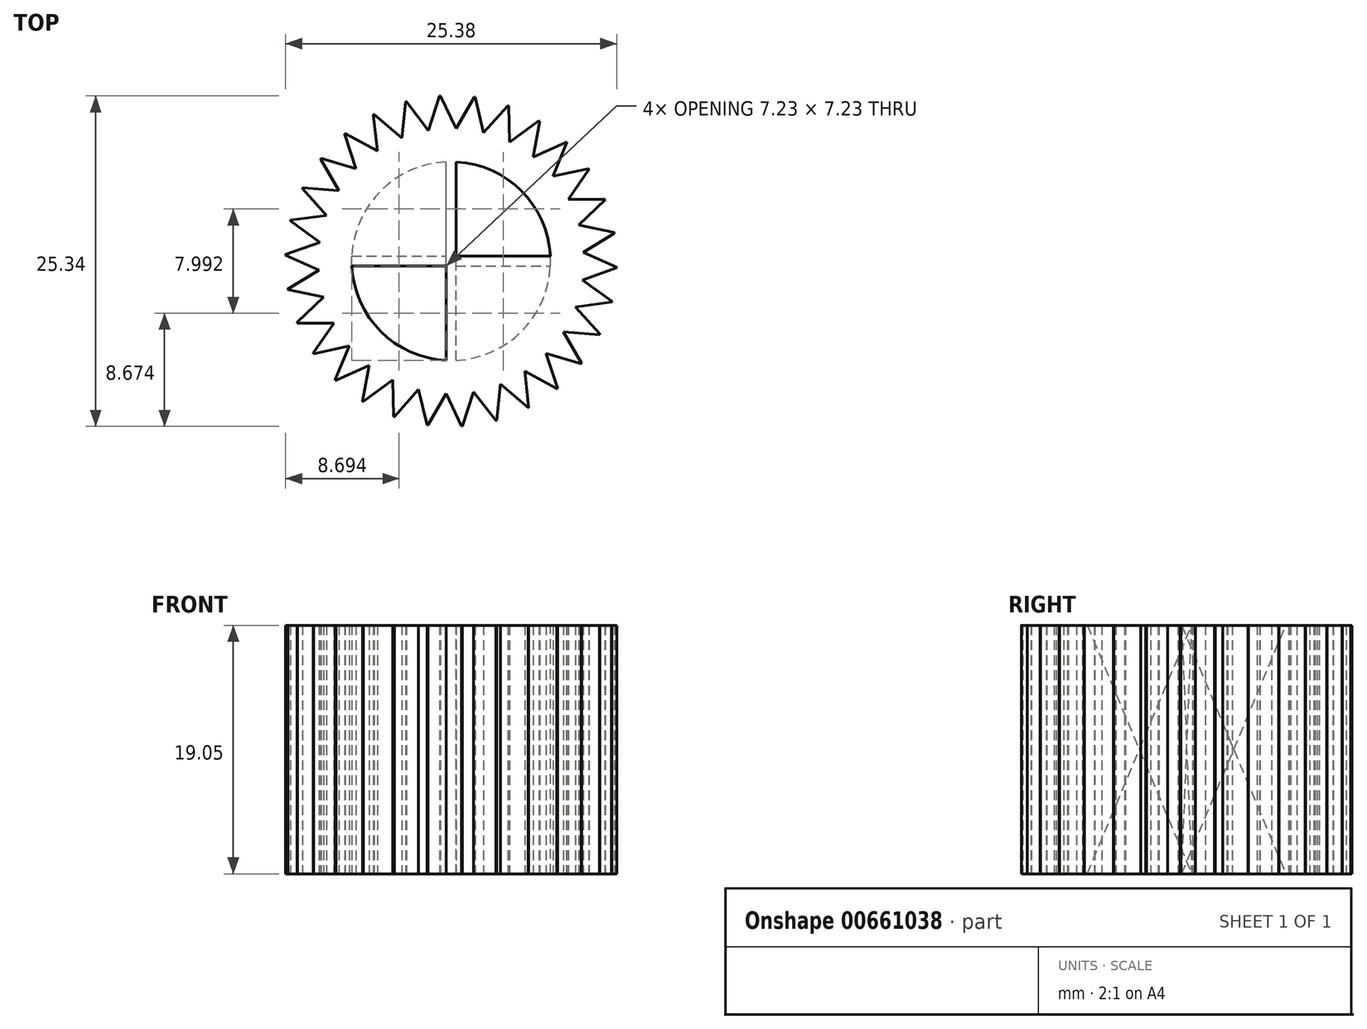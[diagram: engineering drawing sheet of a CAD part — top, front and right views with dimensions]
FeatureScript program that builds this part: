
annotation { "Feature Type Name" : "Feature", "Feature Type Description" : "" }
export const myFeature = defineFeature(function(context is Context, id is Id, definition is map)
    precondition{}
    {
        {
            var Q0;
            Q0=qCreatedBy(makeId("Top.planeOp"),FACE);
            var sketch = newSketch(context, id + "F0", { "sketchPlane" : qUnion([Q0])});
            skCircle(sketch, "E0", {"center": v(0, 0) * mm, "radius": 12.7 * mm});
            skCircle(sketch, "E1", {"center": v(0, 0) * mm, "radius": 10.16 * mm});
            skLineSegment(sketch, "E2", {"start": v(-3.43, 12.23) * mm, "end": v(-1.73, 10.01) * mm});
            skLineSegment(sketch, "E3", {"start": v(-1.73, 10.01) * mm, "end": v(-0.87, 12.67) * mm});
            skLineSegment(sketch, "E4.1.0", {"start": v(-3.78, 9.43) * mm, "end": v(-3.49, 12.21) * mm});
            skLineSegment(sketch, "E4.1.1", {"start": v(-5.9, 11.25) * mm, "end": v(-3.78, 9.43) * mm});
            skLineSegment(sketch, "E4.2.0", {"start": v(-5.65, 8.44) * mm, "end": v(-5.95, 11.22) * mm});
            skLineSegment(sketch, "E4.2.1", {"start": v(-8.11, 9.77) * mm, "end": v(-5.65, 8.44) * mm});
            skLineSegment(sketch, "E4.3.0", {"start": v(-7.29, 7.08) * mm, "end": v(-8.15, 9.74) * mm});
            skLineSegment(sketch, "E4.3.1", {"start": v(-9.96, 7.87) * mm, "end": v(-7.29, 7.08) * mm});
            skLineSegment(sketch, "E4.4.0", {"start": v(-8.6, 5.41) * mm, "end": v(-10, 7.83) * mm});
            skLineSegment(sketch, "E4.4.1", {"start": v(-11.38, 5.63) * mm, "end": v(-8.6, 5.41) * mm});
            skLineSegment(sketch, "E4.5.0", {"start": v(-9.54, 3.5) * mm, "end": v(-11.4, 5.58) * mm});
            skLineSegment(sketch, "E4.5.1", {"start": v(-12.3, 3.14) * mm, "end": v(-9.54, 3.5) * mm});
            skLineSegment(sketch, "E4.6.0", {"start": v(-10.06, 1.45) * mm, "end": v(-12.32, 3.09) * mm});
            skLineSegment(sketch, "E4.6.1", {"start": v(-12.69, 0.51) * mm, "end": v(-10.06, 1.45) * mm});
            skLineSegment(sketch, "E4.7.0", {"start": v(-10.14, -0.68) * mm, "end": v(-12.7, 0.46) * mm});
            skLineSegment(sketch, "E4.7.1", {"start": v(-12.52, -2.14) * mm, "end": v(-10.14, -0.68) * mm});
            skLineSegment(sketch, "E4.8.0", {"start": v(-9.78, -2.77) * mm, "end": v(-12.5, -2.2) * mm});
            skLineSegment(sketch, "E4.8.1", {"start": v(-11.8, -4.7) * mm, "end": v(-9.78, -2.77) * mm});
            skLineSegment(sketch, "E4.9.0", {"start": v(-8.99, -4.74) * mm, "end": v(-11.78, -4.74) * mm});
            skLineSegment(sketch, "E4.9.1", {"start": v(-10.57, -7.04) * mm, "end": v(-8.99, -4.74) * mm});
            skLineSegment(sketch, "E4.10.0", {"start": v(-7.8, -6.5) * mm, "end": v(-10.54, -7.1) * mm});
            skLineSegment(sketch, "E4.10.1", {"start": v(-8.87, -9.09) * mm, "end": v(-7.8, -6.5) * mm});
            skLineSegment(sketch, "E4.11.0", {"start": v(-6.28, -7.99) * mm, "end": v(-8.83, -9.13) * mm});
            skLineSegment(sketch, "E4.11.1", {"start": v(-6.79, -10.73) * mm, "end": v(-6.28, -7.99) * mm});
            skLineSegment(sketch, "E4.12.0", {"start": v(-4.48, -9.12) * mm, "end": v(-6.74, -10.76) * mm});
            skLineSegment(sketch, "E4.12.1", {"start": v(-4.4, -11.91) * mm, "end": v(-4.48, -9.12) * mm});
            skLineSegment(sketch, "E4.13.0", {"start": v(-2.5, -9.85) * mm, "end": v(-4.36, -11.93) * mm});
            skLineSegment(sketch, "E4.13.1", {"start": v(-1.84, -12.57) * mm, "end": v(-2.5, -9.85) * mm});
            skLineSegment(sketch, "E4.14.0", {"start": v(-0.39, -10.15) * mm, "end": v(-1.78, -12.57) * mm});
            skLineSegment(sketch, "E4.14.1", {"start": v(0.82, -12.67) * mm, "end": v(-0.39, -10.15) * mm});
            skLineSegment(sketch, "E4.15.0", {"start": v(1.73, -10.01) * mm, "end": v(0.87, -12.67) * mm});
            skLineSegment(sketch, "E4.15.1", {"start": v(3.43, -12.23) * mm, "end": v(1.73, -10.01) * mm});
            skLineSegment(sketch, "E4.16.0", {"start": v(3.78, -9.43) * mm, "end": v(3.49, -12.21) * mm});
            skLineSegment(sketch, "E4.16.1", {"start": v(5.9, -11.25) * mm, "end": v(3.78, -9.43) * mm});
            skLineSegment(sketch, "E4.17.0", {"start": v(5.65, -8.44) * mm, "end": v(5.95, -11.22) * mm});
            skLineSegment(sketch, "E4.17.1", {"start": v(8.11, -9.77) * mm, "end": v(5.65, -8.44) * mm});
            skLineSegment(sketch, "E4.18.0", {"start": v(7.29, -7.08) * mm, "end": v(8.15, -9.74) * mm});
            skLineSegment(sketch, "E4.18.1", {"start": v(9.96, -7.87) * mm, "end": v(7.29, -7.08) * mm});
            skLineSegment(sketch, "E4.19.0", {"start": v(8.6, -5.41) * mm, "end": v(10, -7.83) * mm});
            skLineSegment(sketch, "E4.19.1", {"start": v(11.38, -5.63) * mm, "end": v(8.6, -5.41) * mm});
            skLineSegment(sketch, "E4.20.0", {"start": v(9.54, -3.5) * mm, "end": v(11.4, -5.58) * mm});
            skLineSegment(sketch, "E4.20.1", {"start": v(12.3, -3.14) * mm, "end": v(9.54, -3.5) * mm});
            skLineSegment(sketch, "E4.21.0", {"start": v(10.06, -1.45) * mm, "end": v(12.32, -3.09) * mm});
            skLineSegment(sketch, "E4.21.1", {"start": v(12.69, -0.51) * mm, "end": v(10.06, -1.45) * mm});
            skLineSegment(sketch, "E4.22.0", {"start": v(10.14, 0.68) * mm, "end": v(12.7, -0.46) * mm});
            skLineSegment(sketch, "E4.22.1", {"start": v(12.52, 2.14) * mm, "end": v(10.14, 0.68) * mm});
            skLineSegment(sketch, "E4.23.0", {"start": v(9.78, 2.77) * mm, "end": v(12.5, 2.2) * mm});
            skLineSegment(sketch, "E4.23.1", {"start": v(11.8, 4.7) * mm, "end": v(9.78, 2.77) * mm});
            skLineSegment(sketch, "E4.24.0", {"start": v(8.99, 4.74) * mm, "end": v(11.78, 4.74) * mm});
            skLineSegment(sketch, "E4.24.1", {"start": v(10.57, 7.04) * mm, "end": v(8.99, 4.74) * mm});
            skLineSegment(sketch, "E5.1.25.0", {"start": v(7.8, 6.5) * mm, "end": v(10.54, 7.1) * mm});
            skLineSegment(sketch, "E5.3.25.0", {"start": v(8.87, 9.09) * mm, "end": v(7.8, 6.5) * mm});
            skLineSegment(sketch, "E5.1.26.0", {"start": v(6.28, 7.99) * mm, "end": v(8.83, 9.13) * mm});
            skLineSegment(sketch, "E5.3.26.0", {"start": v(6.79, 10.73) * mm, "end": v(6.28, 7.99) * mm});
            skLineSegment(sketch, "E5.1.27.0", {"start": v(4.48, 9.12) * mm, "end": v(6.74, 10.76) * mm});
            skLineSegment(sketch, "E5.3.27.0", {"start": v(4.4, 11.91) * mm, "end": v(4.48, 9.12) * mm});
            skLineSegment(sketch, "E5.1.28.0", {"start": v(2.5, 9.85) * mm, "end": v(4.36, 11.93) * mm});
            skLineSegment(sketch, "E5.3.28.0", {"start": v(1.84, 12.57) * mm, "end": v(2.5, 9.85) * mm});
            skLineSegment(sketch, "E5.1.29.0", {"start": v(0.39, 10.15) * mm, "end": v(1.78, 12.57) * mm});
            skLineSegment(sketch, "E5.3.29.0", {"start": v(-0.82, 12.67) * mm, "end": v(0.39, 10.15) * mm});
            skSolve(sketch);
        }
        {
            var Q0;
            {var subQ0=sQuery(id+"F0.wireOp",EDGE,"E1");var subQ18=makeQuery(id+"F0.imprint","INTERSECT",VERTEX,{"derivedFrom":[subQ0,sQuery(id+"F0.wireOp",EDGE,"E4.22.0"),sQuery(id+"F0.wireOp",EDGE,"E4.22.1")]});Q0=makeQuery(id+"F0.imprint","IMPRINT",FACE,{"disambiguationData":[TD([[makeQuery(id+"F0.imprint","IMPRINT",EDGE,{"disambiguationData":[TD([[subQ18,-1.0]])],"derivedFrom":subQ0}),1.0]])]});}
            var Q1;
            {var subQ0=sQuery(id+"F0.wireOp",EDGE,"E5.3.28.0");Q1=makeQuery(id+"F0.imprint","IMPRINT",FACE,{"disambiguationData":[TD([[makeQuery(id+"F0.imprint","IMPRINT",EDGE,{"derivedFrom":subQ0}),-1.0]])]});}
            var Q2;
            {var subQ0=sQuery(id+"F0.wireOp",EDGE,"E5.3.27.0");Q2=makeQuery(id+"F0.imprint","IMPRINT",FACE,{"disambiguationData":[TD([[makeQuery(id+"F0.imprint","IMPRINT",EDGE,{"derivedFrom":subQ0}),-1.0]])]});}
            var Q3;
            {var subQ0=sQuery(id+"F0.wireOp",EDGE,"E5.3.26.0");Q3=makeQuery(id+"F0.imprint","IMPRINT",FACE,{"disambiguationData":[TD([[makeQuery(id+"F0.imprint","IMPRINT",EDGE,{"derivedFrom":subQ0}),-1.0]])]});}
            var Q4;
            {var subQ0=sQuery(id+"F0.wireOp",EDGE,"E5.3.25.0");Q4=makeQuery(id+"F0.imprint","IMPRINT",FACE,{"disambiguationData":[TD([[makeQuery(id+"F0.imprint","IMPRINT",EDGE,{"derivedFrom":subQ0}),-1.0]])]});}
            var Q5;
            {var subQ0=sQuery(id+"F0.wireOp",EDGE,"E4.24.1");Q5=makeQuery(id+"F0.imprint","IMPRINT",FACE,{"disambiguationData":[TD([[makeQuery(id+"F0.imprint","IMPRINT",EDGE,{"derivedFrom":subQ0}),-1.0]])]});}
            var Q6;
            {var subQ0=sQuery(id+"F0.wireOp",EDGE,"E4.23.1");Q6=makeQuery(id+"F0.imprint","IMPRINT",FACE,{"disambiguationData":[TD([[makeQuery(id+"F0.imprint","IMPRINT",EDGE,{"derivedFrom":subQ0}),-1.0]])]});}
            var Q7;
            {var subQ0=sQuery(id+"F0.wireOp",EDGE,"E4.22.1");Q7=makeQuery(id+"F0.imprint","IMPRINT",FACE,{"disambiguationData":[TD([[makeQuery(id+"F0.imprint","IMPRINT",EDGE,{"derivedFrom":subQ0}),-1.0]])]});}
            var Q8;
            {var subQ0=sQuery(id+"F0.wireOp",EDGE,"E4.20.1");Q8=makeQuery(id+"F0.imprint","IMPRINT",FACE,{"disambiguationData":[TD([[makeQuery(id+"F0.imprint","IMPRINT",EDGE,{"derivedFrom":subQ0}),-1.0]])]});}
            var Q9;
            {var subQ0=sQuery(id+"F0.wireOp",EDGE,"E4.18.1");Q9=makeQuery(id+"F0.imprint","IMPRINT",FACE,{"disambiguationData":[TD([[makeQuery(id+"F0.imprint","IMPRINT",EDGE,{"derivedFrom":subQ0}),-1.0]])]});}
            var Q10;
            {var subQ0=sQuery(id+"F0.wireOp",EDGE,"E4.17.1");Q10=makeQuery(id+"F0.imprint","IMPRINT",FACE,{"disambiguationData":[TD([[makeQuery(id+"F0.imprint","IMPRINT",EDGE,{"derivedFrom":subQ0}),-1.0]])]});}
            var Q11;
            {var subQ0=sQuery(id+"F0.wireOp",EDGE,"E4.16.1");Q11=makeQuery(id+"F0.imprint","IMPRINT",FACE,{"disambiguationData":[TD([[makeQuery(id+"F0.imprint","IMPRINT",EDGE,{"derivedFrom":subQ0}),-1.0]])]});}
            var Q12;
            {var subQ0=sQuery(id+"F0.wireOp",EDGE,"E4.15.1");Q12=makeQuery(id+"F0.imprint","IMPRINT",FACE,{"disambiguationData":[TD([[makeQuery(id+"F0.imprint","IMPRINT",EDGE,{"derivedFrom":subQ0}),-1.0]])]});}
            var Q13;
            {var subQ0=sQuery(id+"F0.wireOp",EDGE,"E4.14.1");Q13=makeQuery(id+"F0.imprint","IMPRINT",FACE,{"disambiguationData":[TD([[makeQuery(id+"F0.imprint","IMPRINT",EDGE,{"derivedFrom":subQ0}),-1.0]])]});}
            var Q14;
            {var subQ0=sQuery(id+"F0.wireOp",EDGE,"E4.13.1");Q14=makeQuery(id+"F0.imprint","IMPRINT",FACE,{"disambiguationData":[TD([[makeQuery(id+"F0.imprint","IMPRINT",EDGE,{"derivedFrom":subQ0}),-1.0]])]});}
            var Q15;
            {var subQ0=sQuery(id+"F0.wireOp",EDGE,"E4.12.1");Q15=makeQuery(id+"F0.imprint","IMPRINT",FACE,{"disambiguationData":[TD([[makeQuery(id+"F0.imprint","IMPRINT",EDGE,{"derivedFrom":subQ0}),-1.0]])]});}
            var Q16;
            {var subQ0=sQuery(id+"F0.wireOp",EDGE,"E4.11.1");Q16=makeQuery(id+"F0.imprint","IMPRINT",FACE,{"disambiguationData":[TD([[makeQuery(id+"F0.imprint","IMPRINT",EDGE,{"derivedFrom":subQ0}),-1.0]])]});}
            var Q17;
            {var subQ0=sQuery(id+"F0.wireOp",EDGE,"E4.10.1");Q17=makeQuery(id+"F0.imprint","IMPRINT",FACE,{"disambiguationData":[TD([[makeQuery(id+"F0.imprint","IMPRINT",EDGE,{"derivedFrom":subQ0}),-1.0]])]});}
            var Q18;
            {var subQ0=sQuery(id+"F0.wireOp",EDGE,"E4.9.1");Q18=makeQuery(id+"F0.imprint","IMPRINT",FACE,{"disambiguationData":[TD([[makeQuery(id+"F0.imprint","IMPRINT",EDGE,{"derivedFrom":subQ0}),-1.0]])]});}
            var Q19;
            {var subQ0=sQuery(id+"F0.wireOp",EDGE,"E4.8.1");Q19=makeQuery(id+"F0.imprint","IMPRINT",FACE,{"disambiguationData":[TD([[makeQuery(id+"F0.imprint","IMPRINT",EDGE,{"derivedFrom":subQ0}),-1.0]])]});}
            var Q20;
            {var subQ0=sQuery(id+"F0.wireOp",EDGE,"E4.7.1");Q20=makeQuery(id+"F0.imprint","IMPRINT",FACE,{"disambiguationData":[TD([[makeQuery(id+"F0.imprint","IMPRINT",EDGE,{"derivedFrom":subQ0}),-1.0]])]});}
            var Q21;
            {var subQ0=sQuery(id+"F0.wireOp",EDGE,"E4.3.1");Q21=makeQuery(id+"F0.imprint","IMPRINT",FACE,{"disambiguationData":[TD([[makeQuery(id+"F0.imprint","IMPRINT",EDGE,{"derivedFrom":subQ0}),-1.0]])]});}
            var Q22;
            {var subQ0=sQuery(id+"F0.wireOp",EDGE,"E4.2.1");Q22=makeQuery(id+"F0.imprint","IMPRINT",FACE,{"disambiguationData":[TD([[makeQuery(id+"F0.imprint","IMPRINT",EDGE,{"derivedFrom":subQ0}),-1.0]])]});}
            var Q23;
            {var subQ0=sQuery(id+"F0.wireOp",EDGE,"E4.1.1");Q23=makeQuery(id+"F0.imprint","IMPRINT",FACE,{"disambiguationData":[TD([[makeQuery(id+"F0.imprint","IMPRINT",EDGE,{"derivedFrom":subQ0}),-1.0]])]});}
            var Q24;
            {var subQ0=sQuery(id+"F0.wireOp",EDGE,"E2");Q24=makeQuery(id+"F0.imprint","IMPRINT",FACE,{"disambiguationData":[TD([[makeQuery(id+"F0.imprint","IMPRINT",EDGE,{"derivedFrom":subQ0}),-1.0]])]});}
            var Q25;
            {var subQ0=sQuery(id+"F0.wireOp",EDGE,"E3");Q25=makeQuery(id+"F0.imprint","IMPRINT",FACE,{"disambiguationData":[TD([[makeQuery(id+"F0.imprint","IMPRINT",EDGE,{"derivedFrom":subQ0}),-1.0]])]});}
            var Q26;
            {var subQ0=sQuery(id+"F0.wireOp",EDGE,"E4.4.1");Q26=makeQuery(id+"F0.imprint","IMPRINT",FACE,{"disambiguationData":[TD([[makeQuery(id+"F0.imprint","IMPRINT",EDGE,{"derivedFrom":subQ0}),-1.0]])]});}
            var Q27;
            {var subQ0=sQuery(id+"F0.wireOp",EDGE,"E4.5.1");Q27=makeQuery(id+"F0.imprint","IMPRINT",FACE,{"disambiguationData":[TD([[makeQuery(id+"F0.imprint","IMPRINT",EDGE,{"derivedFrom":subQ0}),-1.0]])]});}
            var Q28;
            {var subQ0=sQuery(id+"F0.wireOp",EDGE,"E4.6.1");Q28=makeQuery(id+"F0.imprint","IMPRINT",FACE,{"disambiguationData":[TD([[makeQuery(id+"F0.imprint","IMPRINT",EDGE,{"derivedFrom":subQ0}),-1.0]])]});}
            var Q29;
            {var subQ0=sQuery(id+"F0.wireOp",EDGE,"E4.19.1");Q29=makeQuery(id+"F0.imprint","IMPRINT",FACE,{"disambiguationData":[TD([[makeQuery(id+"F0.imprint","IMPRINT",EDGE,{"derivedFrom":subQ0}),-1.0]])]});}
            var Q30;
            {var subQ0=sQuery(id+"F0.wireOp",EDGE,"E4.21.1");Q30=makeQuery(id+"F0.imprint","IMPRINT",FACE,{"disambiguationData":[TD([[makeQuery(id+"F0.imprint","IMPRINT",EDGE,{"derivedFrom":subQ0}),-1.0]])]});}
            extrude(context, id + "F1", {"entities" : qUnion([Q0, Q1, Q2, Q3, Q4, Q5, Q6, Q7, Q8, Q9, Q10, Q11, Q12, Q13, Q14, Q15, Q16, Q17, Q18, Q19, Q20, Q21, Q22, Q23, Q24, Q25, Q26, Q27, Q28, Q29, Q30]), "depth" : 19.05 * mm, "offsetDistance" : 25.4 * mm});
        }
        {
            var Q0;
            Q0=makeQuery(id+"F1.opExtrude","CAP_FACE",FACE,{"disambiguationData":[OSD([sQuery(id+"F0.wireOp",EDGE,"E0"),sQuery(id+"F0.wireOp",EDGE,"E2"),sQuery(id+"F0.wireOp",EDGE,"E3"),sQuery(id+"F0.wireOp",EDGE,"E4.1.0"),sQuery(id+"F0.wireOp",EDGE,"E4.1.1"),sQuery(id+"F0.wireOp",EDGE,"E4.2.0"),sQuery(id+"F0.wireOp",EDGE,"E4.2.1"),sQuery(id+"F0.wireOp",EDGE,"E4.3.0"),sQuery(id+"F0.wireOp",EDGE,"E4.3.1"),sQuery(id+"F0.wireOp",EDGE,"E4.4.0"),sQuery(id+"F0.wireOp",EDGE,"E4.4.1"),sQuery(id+"F0.wireOp",EDGE,"E4.5.0"),sQuery(id+"F0.wireOp",EDGE,"E4.5.1"),sQuery(id+"F0.wireOp",EDGE,"E4.6.0"),sQuery(id+"F0.wireOp",EDGE,"E4.6.1"),sQuery(id+"F0.wireOp",EDGE,"E4.7.0"),sQuery(id+"F0.wireOp",EDGE,"E4.7.1"),sQuery(id+"F0.wireOp",EDGE,"E4.8.0"),sQuery(id+"F0.wireOp",EDGE,"E4.8.1"),sQuery(id+"F0.wireOp",EDGE,"E4.9.0"),sQuery(id+"F0.wireOp",EDGE,"E4.9.1"),sQuery(id+"F0.wireOp",EDGE,"E4.10.0"),sQuery(id+"F0.wireOp",EDGE,"E4.10.1"),sQuery(id+"F0.wireOp",EDGE,"E4.11.0"),sQuery(id+"F0.wireOp",EDGE,"E4.11.1"),sQuery(id+"F0.wireOp",EDGE,"E4.12.0"),sQuery(id+"F0.wireOp",EDGE,"E4.12.1"),sQuery(id+"F0.wireOp",EDGE,"E4.13.0"),sQuery(id+"F0.wireOp",EDGE,"E4.13.1"),sQuery(id+"F0.wireOp",EDGE,"E4.14.0"),sQuery(id+"F0.wireOp",EDGE,"E4.14.1"),sQuery(id+"F0.wireOp",EDGE,"E4.15.0"),sQuery(id+"F0.wireOp",EDGE,"E4.15.1"),sQuery(id+"F0.wireOp",EDGE,"E4.16.0"),sQuery(id+"F0.wireOp",EDGE,"E4.16.1"),sQuery(id+"F0.wireOp",EDGE,"E4.17.0"),sQuery(id+"F0.wireOp",EDGE,"E4.17.1"),sQuery(id+"F0.wireOp",EDGE,"E4.18.0"),sQuery(id+"F0.wireOp",EDGE,"E4.18.1"),sQuery(id+"F0.wireOp",EDGE,"E4.19.0"),sQuery(id+"F0.wireOp",EDGE,"E4.19.1"),sQuery(id+"F0.wireOp",EDGE,"E4.20.0"),sQuery(id+"F0.wireOp",EDGE,"E4.20.1"),sQuery(id+"F0.wireOp",EDGE,"E4.21.0"),sQuery(id+"F0.wireOp",EDGE,"E4.21.1"),sQuery(id+"F0.wireOp",EDGE,"E4.22.0"),sQuery(id+"F0.wireOp",EDGE,"E4.22.1"),sQuery(id+"F0.wireOp",EDGE,"E4.23.0"),sQuery(id+"F0.wireOp",EDGE,"E4.23.1"),sQuery(id+"F0.wireOp",EDGE,"E4.24.0"),sQuery(id+"F0.wireOp",EDGE,"E4.24.1"),sQuery(id+"F0.wireOp",EDGE,"E5.1.25.0"),sQuery(id+"F0.wireOp",EDGE,"E5.3.25.0"),sQuery(id+"F0.wireOp",EDGE,"E5.1.26.0"),sQuery(id+"F0.wireOp",EDGE,"E5.3.26.0"),sQuery(id+"F0.wireOp",EDGE,"E5.1.27.0"),sQuery(id+"F0.wireOp",EDGE,"E5.3.27.0"),sQuery(id+"F0.wireOp",EDGE,"E5.1.28.0"),sQuery(id+"F0.wireOp",EDGE,"E5.3.28.0"),sQuery(id+"F0.wireOp",EDGE,"E5.1.29.0"),sQuery(id+"F0.wireOp",EDGE,"E5.3.29.0")])],"isStart":false});
            var sketch = newSketch(context, id + "F2", { "sketchPlane" : qUnion([Q0])});
            skCircle(sketch, "E6", {"center": v(0, 0) * mm, "radius": 7.62 * mm});
            skLineSegment(sketch, "E7", {"start": v(-7.61, -0.38) * mm, "end": v(-0.38, -0.38) * mm});
            skLineSegment(sketch, "E8", {"start": v(-0.38, -0.38) * mm, "end": v(-0.38, -7.61) * mm});
            skLineSegment(sketch, "E9", {"start": v(0, -7.62) * mm, "end": v(0, 0) * mm});
            skLineSegment(sketch, "E10", {"start": v(-7.62, 0) * mm, "end": v(0, 0) * mm});
            skSolve(sketch);
        }
        {
            var Q0;
            Q0=makeQuery(id+"F1.opExtrude","CAP_FACE",FACE,{"disambiguationData":[OSD([sQuery(id+"F0.wireOp",EDGE,"E0"),sQuery(id+"F0.wireOp",EDGE,"E2"),sQuery(id+"F0.wireOp",EDGE,"E3"),sQuery(id+"F0.wireOp",EDGE,"E4.1.0"),sQuery(id+"F0.wireOp",EDGE,"E4.1.1"),sQuery(id+"F0.wireOp",EDGE,"E4.2.0"),sQuery(id+"F0.wireOp",EDGE,"E4.2.1"),sQuery(id+"F0.wireOp",EDGE,"E4.3.0"),sQuery(id+"F0.wireOp",EDGE,"E4.3.1"),sQuery(id+"F0.wireOp",EDGE,"E4.4.0"),sQuery(id+"F0.wireOp",EDGE,"E4.4.1"),sQuery(id+"F0.wireOp",EDGE,"E4.5.0"),sQuery(id+"F0.wireOp",EDGE,"E4.5.1"),sQuery(id+"F0.wireOp",EDGE,"E4.6.0"),sQuery(id+"F0.wireOp",EDGE,"E4.6.1"),sQuery(id+"F0.wireOp",EDGE,"E4.7.0"),sQuery(id+"F0.wireOp",EDGE,"E4.7.1"),sQuery(id+"F0.wireOp",EDGE,"E4.8.0"),sQuery(id+"F0.wireOp",EDGE,"E4.8.1"),sQuery(id+"F0.wireOp",EDGE,"E4.9.0"),sQuery(id+"F0.wireOp",EDGE,"E4.9.1"),sQuery(id+"F0.wireOp",EDGE,"E4.10.0"),sQuery(id+"F0.wireOp",EDGE,"E4.10.1"),sQuery(id+"F0.wireOp",EDGE,"E4.11.0"),sQuery(id+"F0.wireOp",EDGE,"E4.11.1"),sQuery(id+"F0.wireOp",EDGE,"E4.12.0"),sQuery(id+"F0.wireOp",EDGE,"E4.12.1"),sQuery(id+"F0.wireOp",EDGE,"E4.13.0"),sQuery(id+"F0.wireOp",EDGE,"E4.13.1"),sQuery(id+"F0.wireOp",EDGE,"E4.14.0"),sQuery(id+"F0.wireOp",EDGE,"E4.14.1"),sQuery(id+"F0.wireOp",EDGE,"E4.15.0"),sQuery(id+"F0.wireOp",EDGE,"E4.15.1"),sQuery(id+"F0.wireOp",EDGE,"E4.16.0"),sQuery(id+"F0.wireOp",EDGE,"E4.16.1"),sQuery(id+"F0.wireOp",EDGE,"E4.17.0"),sQuery(id+"F0.wireOp",EDGE,"E4.17.1"),sQuery(id+"F0.wireOp",EDGE,"E4.18.0"),sQuery(id+"F0.wireOp",EDGE,"E4.18.1"),sQuery(id+"F0.wireOp",EDGE,"E4.19.0"),sQuery(id+"F0.wireOp",EDGE,"E4.19.1"),sQuery(id+"F0.wireOp",EDGE,"E4.20.0"),sQuery(id+"F0.wireOp",EDGE,"E4.20.1"),sQuery(id+"F0.wireOp",EDGE,"E4.21.0"),sQuery(id+"F0.wireOp",EDGE,"E4.21.1"),sQuery(id+"F0.wireOp",EDGE,"E4.22.0"),sQuery(id+"F0.wireOp",EDGE,"E4.22.1"),sQuery(id+"F0.wireOp",EDGE,"E4.23.0"),sQuery(id+"F0.wireOp",EDGE,"E4.23.1"),sQuery(id+"F0.wireOp",EDGE,"E4.24.0"),sQuery(id+"F0.wireOp",EDGE,"E4.24.1"),sQuery(id+"F0.wireOp",EDGE,"E5.1.25.0"),sQuery(id+"F0.wireOp",EDGE,"E5.3.25.0"),sQuery(id+"F0.wireOp",EDGE,"E5.1.26.0"),sQuery(id+"F0.wireOp",EDGE,"E5.3.26.0"),sQuery(id+"F0.wireOp",EDGE,"E5.1.27.0"),sQuery(id+"F0.wireOp",EDGE,"E5.3.27.0"),sQuery(id+"F0.wireOp",EDGE,"E5.1.28.0"),sQuery(id+"F0.wireOp",EDGE,"E5.3.28.0"),sQuery(id+"F0.wireOp",EDGE,"E5.1.29.0"),sQuery(id+"F0.wireOp",EDGE,"E5.3.29.0")])],"isStart":true});
            var sketch = newSketch(context, id + "F3", { "sketchPlane" : qUnion([Q0])});
            skCircle(sketch, "E11", {"center": v(0, 0) * mm, "radius": 7.62 * mm});
            skLineSegment(sketch, "E12", {"start": v(-7.61, -0.38) * mm, "end": v(-0.38, -0.38) * mm});
            skLineSegment(sketch, "E13", {"start": v(-0.38, -0.38) * mm, "end": v(-0.38, -7.61) * mm});
            skLineSegment(sketch, "E14", {"start": v(0, 0) * mm, "end": v(0, -7.62) * mm});
            skLineSegment(sketch, "E15", {"start": v(0, 0) * mm, "end": v(-7.62, 0) * mm});
            skSolve(sketch);
        }
        {
            var Q1;
            {var subQ0=sQuery(id+"F2.wireOp",EDGE,"E7");Q1=makeQuery(id+"F2.imprint","IMPRINT",FACE,{"disambiguationData":[TD([[makeQuery(id+"F2.imprint","IMPRINT",EDGE,{"derivedFrom":subQ0}),-1.0]])]});}
            var Q2;
            {var subQ0=sQuery(id+"F3.wireOp",EDGE,"E12");Q2=makeQuery(id+"F3.imprint","IMPRINT",FACE,{"disambiguationData":[TD([[makeQuery(id+"F3.imprint","IMPRINT",EDGE,{"derivedFrom":subQ0}),-1.0]])]});}
            loft(context, id + "F4", {"operationType" : NewBodyOperationType.REMOVE, "sheetProfilesArray" : [{ "sheetProfileEntities" : qUnion([Q1]) }, { "sheetProfileEntities" : qUnion([Q2]) }]});
        }
        {
            var Q0;
            Q0=makeQuery(id+"F1.opExtrude","CAP_FACE",FACE,{"disambiguationData":[OSD([sQuery(id+"F0.wireOp",EDGE,"E0"),sQuery(id+"F0.wireOp",EDGE,"E2"),sQuery(id+"F0.wireOp",EDGE,"E3"),sQuery(id+"F0.wireOp",EDGE,"E4.1.0"),sQuery(id+"F0.wireOp",EDGE,"E4.1.1"),sQuery(id+"F0.wireOp",EDGE,"E4.2.0"),sQuery(id+"F0.wireOp",EDGE,"E4.2.1"),sQuery(id+"F0.wireOp",EDGE,"E4.3.0"),sQuery(id+"F0.wireOp",EDGE,"E4.3.1"),sQuery(id+"F0.wireOp",EDGE,"E4.4.0"),sQuery(id+"F0.wireOp",EDGE,"E4.4.1"),sQuery(id+"F0.wireOp",EDGE,"E4.5.0"),sQuery(id+"F0.wireOp",EDGE,"E4.5.1"),sQuery(id+"F0.wireOp",EDGE,"E4.6.0"),sQuery(id+"F0.wireOp",EDGE,"E4.6.1"),sQuery(id+"F0.wireOp",EDGE,"E4.7.0"),sQuery(id+"F0.wireOp",EDGE,"E4.7.1"),sQuery(id+"F0.wireOp",EDGE,"E4.8.0"),sQuery(id+"F0.wireOp",EDGE,"E4.8.1"),sQuery(id+"F0.wireOp",EDGE,"E4.9.0"),sQuery(id+"F0.wireOp",EDGE,"E4.9.1"),sQuery(id+"F0.wireOp",EDGE,"E4.10.0"),sQuery(id+"F0.wireOp",EDGE,"E4.10.1"),sQuery(id+"F0.wireOp",EDGE,"E4.11.0"),sQuery(id+"F0.wireOp",EDGE,"E4.11.1"),sQuery(id+"F0.wireOp",EDGE,"E4.12.0"),sQuery(id+"F0.wireOp",EDGE,"E4.12.1"),sQuery(id+"F0.wireOp",EDGE,"E4.13.0"),sQuery(id+"F0.wireOp",EDGE,"E4.13.1"),sQuery(id+"F0.wireOp",EDGE,"E4.14.0"),sQuery(id+"F0.wireOp",EDGE,"E4.14.1"),sQuery(id+"F0.wireOp",EDGE,"E4.15.0"),sQuery(id+"F0.wireOp",EDGE,"E4.15.1"),sQuery(id+"F0.wireOp",EDGE,"E4.16.0"),sQuery(id+"F0.wireOp",EDGE,"E4.16.1"),sQuery(id+"F0.wireOp",EDGE,"E4.17.0"),sQuery(id+"F0.wireOp",EDGE,"E4.17.1"),sQuery(id+"F0.wireOp",EDGE,"E4.18.0"),sQuery(id+"F0.wireOp",EDGE,"E4.18.1"),sQuery(id+"F0.wireOp",EDGE,"E4.19.0"),sQuery(id+"F0.wireOp",EDGE,"E4.19.1"),sQuery(id+"F0.wireOp",EDGE,"E4.20.0"),sQuery(id+"F0.wireOp",EDGE,"E4.20.1"),sQuery(id+"F0.wireOp",EDGE,"E4.21.0"),sQuery(id+"F0.wireOp",EDGE,"E4.21.1"),sQuery(id+"F0.wireOp",EDGE,"E4.22.0"),sQuery(id+"F0.wireOp",EDGE,"E4.22.1"),sQuery(id+"F0.wireOp",EDGE,"E4.23.0"),sQuery(id+"F0.wireOp",EDGE,"E4.23.1"),sQuery(id+"F0.wireOp",EDGE,"E4.24.0"),sQuery(id+"F0.wireOp",EDGE,"E4.24.1"),sQuery(id+"F0.wireOp",EDGE,"E5.1.25.0"),sQuery(id+"F0.wireOp",EDGE,"E5.3.25.0"),sQuery(id+"F0.wireOp",EDGE,"E5.1.26.0"),sQuery(id+"F0.wireOp",EDGE,"E5.3.26.0"),sQuery(id+"F0.wireOp",EDGE,"E5.1.27.0"),sQuery(id+"F0.wireOp",EDGE,"E5.3.27.0"),sQuery(id+"F0.wireOp",EDGE,"E5.1.28.0"),sQuery(id+"F0.wireOp",EDGE,"E5.3.28.0"),sQuery(id+"F0.wireOp",EDGE,"E5.1.29.0"),sQuery(id+"F0.wireOp",EDGE,"E5.3.29.0")])],"isStart":false});
            var sketch = newSketch(context, id + "F5", { "sketchPlane" : qUnion([Q0])});
            skCircle(sketch, "E16", {"center": v(0, 0) * mm, "radius": 7.62 * mm});
            skLineSegment(sketch, "E17", {"start": v(0, 0) * mm, "end": v(0, 7.62) * mm});
            skLineSegment(sketch, "E18", {"start": v(0, 0) * mm, "end": v(7.62, 0) * mm});
            skLineSegment(sketch, "E19", {"start": v(7.61, 0.38) * mm, "end": v(0.38, 0.38) * mm});
            skLineSegment(sketch, "E20", {"start": v(0.38, 0.38) * mm, "end": v(0.38, 7.61) * mm});
            skSolve(sketch);
        }
        {
            var Q0;
            Q0=makeQuery(id+"F1.opExtrude","CAP_FACE",FACE,{"disambiguationData":[OSD([sQuery(id+"F0.wireOp",EDGE,"E0"),sQuery(id+"F0.wireOp",EDGE,"E2"),sQuery(id+"F0.wireOp",EDGE,"E3"),sQuery(id+"F0.wireOp",EDGE,"E4.1.0"),sQuery(id+"F0.wireOp",EDGE,"E4.1.1"),sQuery(id+"F0.wireOp",EDGE,"E4.2.0"),sQuery(id+"F0.wireOp",EDGE,"E4.2.1"),sQuery(id+"F0.wireOp",EDGE,"E4.3.0"),sQuery(id+"F0.wireOp",EDGE,"E4.3.1"),sQuery(id+"F0.wireOp",EDGE,"E4.4.0"),sQuery(id+"F0.wireOp",EDGE,"E4.4.1"),sQuery(id+"F0.wireOp",EDGE,"E4.5.0"),sQuery(id+"F0.wireOp",EDGE,"E4.5.1"),sQuery(id+"F0.wireOp",EDGE,"E4.6.0"),sQuery(id+"F0.wireOp",EDGE,"E4.6.1"),sQuery(id+"F0.wireOp",EDGE,"E4.7.0"),sQuery(id+"F0.wireOp",EDGE,"E4.7.1"),sQuery(id+"F0.wireOp",EDGE,"E4.8.0"),sQuery(id+"F0.wireOp",EDGE,"E4.8.1"),sQuery(id+"F0.wireOp",EDGE,"E4.9.0"),sQuery(id+"F0.wireOp",EDGE,"E4.9.1"),sQuery(id+"F0.wireOp",EDGE,"E4.10.0"),sQuery(id+"F0.wireOp",EDGE,"E4.10.1"),sQuery(id+"F0.wireOp",EDGE,"E4.11.0"),sQuery(id+"F0.wireOp",EDGE,"E4.11.1"),sQuery(id+"F0.wireOp",EDGE,"E4.12.0"),sQuery(id+"F0.wireOp",EDGE,"E4.12.1"),sQuery(id+"F0.wireOp",EDGE,"E4.13.0"),sQuery(id+"F0.wireOp",EDGE,"E4.13.1"),sQuery(id+"F0.wireOp",EDGE,"E4.14.0"),sQuery(id+"F0.wireOp",EDGE,"E4.14.1"),sQuery(id+"F0.wireOp",EDGE,"E4.15.0"),sQuery(id+"F0.wireOp",EDGE,"E4.15.1"),sQuery(id+"F0.wireOp",EDGE,"E4.16.0"),sQuery(id+"F0.wireOp",EDGE,"E4.16.1"),sQuery(id+"F0.wireOp",EDGE,"E4.17.0"),sQuery(id+"F0.wireOp",EDGE,"E4.17.1"),sQuery(id+"F0.wireOp",EDGE,"E4.18.0"),sQuery(id+"F0.wireOp",EDGE,"E4.18.1"),sQuery(id+"F0.wireOp",EDGE,"E4.19.0"),sQuery(id+"F0.wireOp",EDGE,"E4.19.1"),sQuery(id+"F0.wireOp",EDGE,"E4.20.0"),sQuery(id+"F0.wireOp",EDGE,"E4.20.1"),sQuery(id+"F0.wireOp",EDGE,"E4.21.0"),sQuery(id+"F0.wireOp",EDGE,"E4.21.1"),sQuery(id+"F0.wireOp",EDGE,"E4.22.0"),sQuery(id+"F0.wireOp",EDGE,"E4.22.1"),sQuery(id+"F0.wireOp",EDGE,"E4.23.0"),sQuery(id+"F0.wireOp",EDGE,"E4.23.1"),sQuery(id+"F0.wireOp",EDGE,"E4.24.0"),sQuery(id+"F0.wireOp",EDGE,"E4.24.1"),sQuery(id+"F0.wireOp",EDGE,"E5.1.25.0"),sQuery(id+"F0.wireOp",EDGE,"E5.3.25.0"),sQuery(id+"F0.wireOp",EDGE,"E5.1.26.0"),sQuery(id+"F0.wireOp",EDGE,"E5.3.26.0"),sQuery(id+"F0.wireOp",EDGE,"E5.1.27.0"),sQuery(id+"F0.wireOp",EDGE,"E5.3.27.0"),sQuery(id+"F0.wireOp",EDGE,"E5.1.28.0"),sQuery(id+"F0.wireOp",EDGE,"E5.3.28.0"),sQuery(id+"F0.wireOp",EDGE,"E5.1.29.0"),sQuery(id+"F0.wireOp",EDGE,"E5.3.29.0")])],"isStart":true});
            var sketch = newSketch(context, id + "F6", { "sketchPlane" : qUnion([Q0])});
            skCircle(sketch, "E21", {"center": v(0, 0) * mm, "radius": 7.62 * mm});
            skLineSegment(sketch, "E22", {"start": v(0, 0) * mm, "end": v(7.62, 0) * mm});
            skLineSegment(sketch, "E23", {"start": v(0, 0) * mm, "end": v(0, 7.62) * mm});
            skLineSegment(sketch, "E24", {"start": v(0.38, 7.61) * mm, "end": v(0.38, 0.38) * mm});
            skLineSegment(sketch, "E25", {"start": v(0.38, 0.38) * mm, "end": v(7.61, 0.38) * mm});
            skSolve(sketch);
        }
        {
            var Q1;
            {var subQ0=sQuery(id+"F6.wireOp",EDGE,"E24");Q1=makeQuery(id+"F6.imprint","IMPRINT",FACE,{"disambiguationData":[TD([[makeQuery(id+"F6.imprint","IMPRINT",EDGE,{"derivedFrom":subQ0}),1.0]])]});}
            var Q2;
            {var subQ0=sQuery(id+"F5.wireOp",EDGE,"E19");Q2=makeQuery(id+"F5.imprint","IMPRINT",FACE,{"disambiguationData":[TD([[makeQuery(id+"F5.imprint","IMPRINT",EDGE,{"derivedFrom":subQ0}),-1.0]])]});}
            loft(context, id + "F7", {"operationType" : NewBodyOperationType.REMOVE, "sheetProfilesArray" : [{ "sheetProfileEntities" : qUnion([Q1]) }, { "sheetProfileEntities" : qUnion([Q2]) }]});
        }
    });
